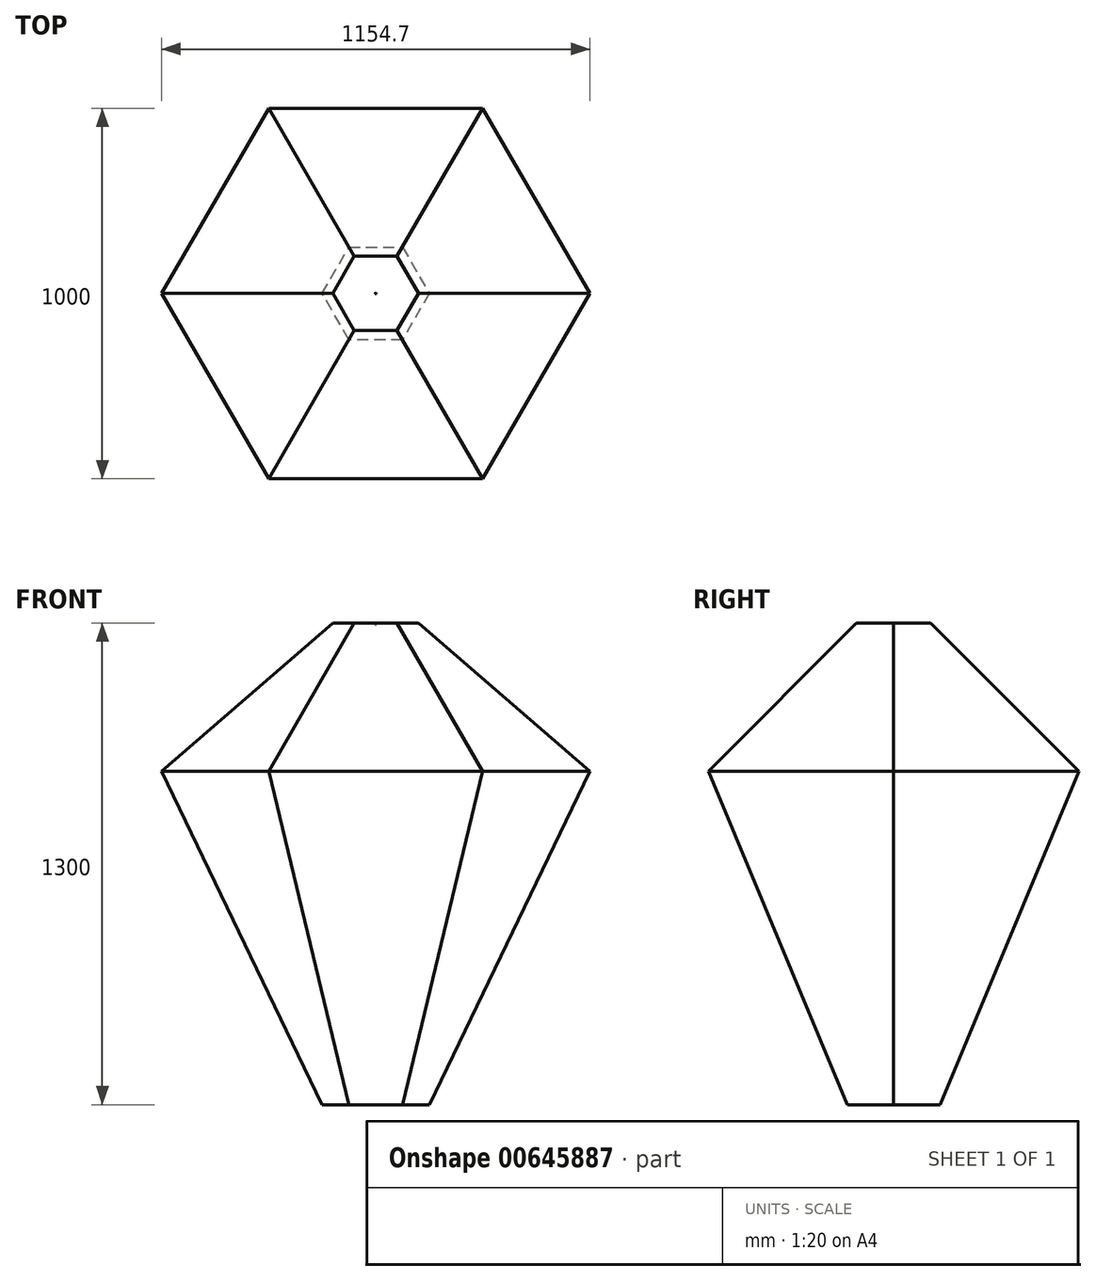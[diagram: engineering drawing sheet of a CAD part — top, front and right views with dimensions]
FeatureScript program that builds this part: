
annotation { "Feature Type Name" : "Feature", "Feature Type Description" : "" }
export const myFeature = defineFeature(function(context is Context, id is Id, definition is map)
    precondition{}
    {
        {
            assignVariable(context, id + "F0", {"name" : "Scale", "anyValue" : 1});
        }
        {
            var Q0;
            Q0=qCreatedBy(makeId("Top.planeOp"),FACE);
            var sketch = newSketch(context, id + "F1", { "sketchPlane" : qUnion([Q0])});
            skCircle(sketch, "E0.cCircle", {"center": v(0, 0) * mm, "radius": 500 * mm, "construction": true});
            skLineSegment(sketch, "E0.0", {"start": v(-288.68, 500) * mm, "end": v(288.68, 500) * mm});
            skLineSegment(sketch, "E0.1", {"start": v(288.68, 500) * mm, "end": v(577.35, 0) * mm});
            skLineSegment(sketch, "E0.2", {"start": v(577.35, 0) * mm, "end": v(288.68, -500) * mm});
            skLineSegment(sketch, "E0.3", {"start": v(288.68, -500) * mm, "end": v(-288.68, -500) * mm});
            skLineSegment(sketch, "E0.4", {"start": v(-288.68, -500) * mm, "end": v(-577.35, 0) * mm});
            skLineSegment(sketch, "E0.5", {"start": v(-577.35, 0) * mm, "end": v(-288.68, 500) * mm});
            skPoint(sketch, "E0.0.midPoint", {"position": v(0, 500) * mm});
            skSolve(sketch);
        }
        {
            var Q0;
            Q0=qCreatedBy(makeId("Top.planeOp"),FACE);
            cPlane(context, id + "F2", {"entities" : qUnion([Q0]), "cplaneType" : CPlaneType.OFFSET, "offset" : getVariable(context, 'Scale') * 400 * mm, "width" : 150 * mm, "height" : 150 * mm});
        }
        {
            var Q0;
            Q0=qCreatedBy(id+"F2.planeOp",FACE);
            var sketch = newSketch(context, id + "F3", { "sketchPlane" : qUnion([Q0])});
            skCircle(sketch, "E1.cCircle", {"center": v(0, 0) * mm, "radius": 100 * mm, "construction": true});
            skLineSegment(sketch, "E1.0", {"start": v(-57.74, 100) * mm, "end": v(57.74, 100) * mm});
            skLineSegment(sketch, "E1.1", {"start": v(57.74, 100) * mm, "end": v(115.47, 0) * mm});
            skLineSegment(sketch, "E1.2", {"start": v(115.47, 0) * mm, "end": v(57.74, -100) * mm});
            skLineSegment(sketch, "E1.3", {"start": v(57.74, -100) * mm, "end": v(-57.74, -100) * mm});
            skLineSegment(sketch, "E1.4", {"start": v(-57.74, -100) * mm, "end": v(-115.47, 0) * mm});
            skLineSegment(sketch, "E1.5", {"start": v(-115.47, 0) * mm, "end": v(-57.74, 100) * mm});
            skPoint(sketch, "E1.0.midPoint", {"position": v(0, 100) * mm});
            skSolve(sketch);
        }
        {
            var Q0;
            Q0=qCreatedBy(makeId("Top.planeOp"),FACE);
            cPlane(context, id + "F4", {"entities" : qUnion([Q0]), "cplaneType" : CPlaneType.OFFSET, "offset" : getVariable(context, 'Scale') * 900 * mm, "oppositeDirection" : true, "width" : 150 * mm, "height" : 150 * mm});
        }
        {
            var Q0;
            Q0=qCreatedBy(id+"F4.planeOp",FACE);
            var sketch = newSketch(context, id + "F5", { "sketchPlane" : qUnion([Q0])});
            skCircle(sketch, "E2.cCircle", {"center": v(0, 0) * mm, "radius": 125 * mm, "construction": true});
            skLineSegment(sketch, "E2.0", {"start": v(72.17, -125) * mm, "end": v(-72.17, -125) * mm});
            skLineSegment(sketch, "E2.1", {"start": v(-72.17, -125) * mm, "end": v(-144.34, 0) * mm});
            skLineSegment(sketch, "E2.2", {"start": v(-144.34, 0) * mm, "end": v(-72.17, 125) * mm});
            skLineSegment(sketch, "E2.3", {"start": v(-72.17, 125) * mm, "end": v(72.17, 125) * mm});
            skLineSegment(sketch, "E2.4", {"start": v(72.17, 125) * mm, "end": v(144.34, 0) * mm});
            skLineSegment(sketch, "E2.5", {"start": v(144.34, 0) * mm, "end": v(72.17, -125) * mm});
            skPoint(sketch, "E2.0.midPoint", {"position": v(0, -125) * mm});
            skSolve(sketch);
        }
        {
            var Q0;
            Q0=makeQuery(id+"F1.imprint","IMPRINT",FACE,{"disambiguationData":[TD([[makeQuery(id+"F1.imprint","IMPRINT",EDGE,{"derivedFrom":sQuery(id+"F1.wireOp",EDGE,"E0.0")}),-1.0]])]});
            var Q1;
            Q1=makeQuery(id+"F3.imprint","IMPRINT",FACE,{"disambiguationData":[TD([[makeQuery(id+"F3.imprint","IMPRINT",EDGE,{"derivedFrom":sQuery(id+"F3.wireOp",EDGE,"E1.0")}),-1.0]])]});
            loft(context, id + "F6", {"sheetProfilesArray" : [{ "sheetProfileEntities" : qUnion([Q0]) }, { "sheetProfileEntities" : qUnion([Q1]) }]});
        }
        {
            var Q1;
            Q1=makeQuery(id+"F5.imprint","IMPRINT",FACE,{"disambiguationData":[TD([[makeQuery(id+"F5.imprint","IMPRINT",EDGE,{"derivedFrom":sQuery(id+"F5.wireOp",EDGE,"E2.0")}),-1.0]])]});
            var Q2;
            Q2=makeQuery(id+"F6.opLoft","CAP_FACE",FACE,{"disambiguationData":[OSD([makeQuery(id+"F1.imprint","IMPRINT",FACE,{"disambiguationData":[TD([[makeQuery(id+"F1.imprint","IMPRINT",EDGE,{"derivedFrom":sQuery(id+"F1.wireOp",EDGE,"E0.0")}),-1.0]])]})])],"isStart":true});
            loft(context, id + "F7", {"operationType" : NewBodyOperationType.ADD, "sheetProfilesArray" : [{ "sheetProfileEntities" : qUnion([Q1]) }, { "sheetProfileEntities" : qUnion([Q2]) }]});
        }
        {
            var Q0;
            Q0=makeQuery(id+"F6.opLoft","CAP_FACE",FACE,{"disambiguationData":[OSD([makeQuery(id+"F3.imprint","IMPRINT",FACE,{"disambiguationData":[TD([[makeQuery(id+"F3.imprint","IMPRINT",EDGE,{"derivedFrom":sQuery(id+"F3.wireOp",EDGE,"E1.0")}),-1.0]])]})])],"isStart":true});
            var sketch = newSketch(context, id + "F8", { "sketchPlane" : qUnion([Q0])});
            skCircle(sketch, "E3", {"center": v(0, 0) * mm, "radius": 1 * mm});
            skSolve(sketch);
        }
        {
            var Q0;
            Q0=makeQuery(id+"F8.imprint","IMPRINT",FACE,{"disambiguationData":[TD([[makeQuery(id+"F8.imprint","IMPRINT",EDGE,{"derivedFrom":sQuery(id+"F8.wireOp",EDGE,"E3")}),1.0]])]});
            extrude(context, id + "F9", {"entities" : qUnion([Q0]), "operationType" : NewBodyOperationType.REMOVE, "oppositeDirection" : true, "depth" : 5 * mm, "offsetDistance" : 25 * mm});
        }
        {
            var Q0;
            Q0=makeQuery(id+"F6.opLoft","CAP_FACE",FACE,{"disambiguationData":[OSD([makeQuery(id+"F3.imprint","IMPRINT",FACE,{"disambiguationData":[TD([[makeQuery(id+"F3.imprint","IMPRINT",EDGE,{"derivedFrom":sQuery(id+"F3.wireOp",EDGE,"E1.0")}),-1.0]])]})])],"isStart":true});
            var sketch = newSketch(context, id + "F10", { "sketchPlane" : qUnion([Q0])});
            skCircle(sketch, "E4", {"center": v(57.74, -100) * mm, "radius": 15 * mm});
            skSolve(sketch);
        }
        {
            var Q0;
            {var subQ0=sQuery(id+"F1.wireOp",EDGE,"E0.3");var subQ1=sQuery(id+"F1.wireOp",EDGE,"E0.2");Q0=makeQuery(id+"F7.boolean.opBoolean","MERGE",VERTEX,{"derivedFrom":[makeQuery(id+"F6.opLoft","MID_CAP_VERTEX",VERTEX,{"disambiguationData":[OSD([subQ1,subQ0])],"capPos":0.0}),makeQuery(id+"F7.opLoft","MID_CAP_VERTEX",VERTEX,{"disambiguationData":[OSD([subQ1,subQ0])],"capPos":1.0})]});}
            var Q1;
            {var subQ0=sQuery(id+"F1.wireOp",EDGE,"E0.4");var subQ1=sQuery(id+"F1.wireOp",EDGE,"E0.3");var subQ2=sQuery(id+"F1.wireOp",EDGE,"E0.2");Q1=makeQuery(id+"F7.boolean.opBoolean","MERGE",EDGE,{"derivedFrom":[makeQuery(id+"F6.opLoft","MID_CAP_EDGE",EDGE,{"disambiguationData":[OSD([subQ2,subQ1,subQ0])],"capPos":0.0}),makeQuery(id+"F7.opLoft","MID_CAP_EDGE",EDGE,{"disambiguationData":[OSD([subQ2,subQ1,subQ0])],"capPos":1.0})]});}
            cPlane(context, id + "F11", {"entities" : qUnion([Q0, Q1]), "cplaneType" : CPlaneType.CURVE_POINT, "offset" : 25 * mm, "width" : 150 * mm, "height" : 150 * mm});
        }
        {
            var Q0;
            Q0=qCreatedBy(id+"F11.planeOp",FACE);
            var sketch = newSketch(context, id + "F12", { "sketchPlane" : qUnion([Q0])});
            skCircle(sketch, "E5", {"center": v(-500, 0) * mm, "radius": 10 * mm});
            skSolve(sketch);
        }
        {
            var Q0;
            Q0=qCreatedBy(makeId("Front.planeOp"),FACE);
            var sketch = newSketch(context, id + "F13", { "sketchPlane" : qUnion([Q0])});
            skLineSegment(sketch, "E6", {"start": v(0, 0) * mm, "end": v(0, 7.92) * mm, "construction": true});
            skSolve(sketch);
        }
        {
            var Q0;
            Q0=makeQuery(id+"F6.opLoft","SWEPT_BODY",BODY,{"disambiguationData":[OSD([makeQuery(id+"F1.imprint","IMPRINT",FACE,{"disambiguationData":[TD([[makeQuery(id+"F1.imprint","IMPRINT",EDGE,{"derivedFrom":sQuery(id+"F1.wireOp",EDGE,"E0.0")}),-1.0]])]}),makeQuery(id+"F3.imprint","IMPRINT",FACE,{"disambiguationData":[TD([[makeQuery(id+"F3.imprint","IMPRINT",EDGE,{"derivedFrom":sQuery(id+"F3.wireOp",EDGE,"E1.0")}),-1.0]])]})])]});
            var Q1;
            Q1=makeQuery(id+"FsViyaIz4K34HAL_1.opSweep","SWEPT_BODY",BODY,{"disambiguationData":[OSD([sQuery(id+"F1.wireOp",EDGE,"E0.2"),sQuery(id+"F1.wireOp",EDGE,"E0.3"),sQuery(id+"F5.wireOp",EDGE,"E2.0"),sQuery(id+"F5.wireOp",EDGE,"E2.5"),sQuery(id+"F10.wireOp",EDGE,"E4")])]});
            var Q2;
            Q2=sQuery(id+"F13.wireOp",EDGE,"E6");
            circularPattern(context, id + "F14", {"entities" : qUnion([Q0, Q1]), "axis" : qUnion([Q2]), "angle" : 360 * degree, "instanceCount" : 6, "equalSpace" : true});
        }
        {
            var Q0;
            Q0=makeQuery(id+"F6.opLoft","MID_CAP_EDGE",EDGE,{"disambiguationData":[OSD([sQuery(id+"F3.wireOp",EDGE,"E1.2"),sQuery(id+"F3.wireOp",EDGE,"E1.3"),sQuery(id+"F3.wireOp",EDGE,"E1.4")])],"capPos":1.0});
            var Q1;
            Q1=makeQuery(id+"F6.opLoft","MID_CAP_VERTEX",VERTEX,{"disambiguationData":[OSD([sQuery(id+"F3.wireOp",EDGE,"E1.2"),sQuery(id+"F3.wireOp",EDGE,"E1.3")])],"capPos":1.0});
            cPlane(context, id + "F15", {"entities" : qUnion([Q0, Q1]), "cplaneType" : CPlaneType.CURVE_POINT, "offset" : 25 * mm, "width" : 150 * mm, "height" : 150 * mm});
        }
        {
            var Q0;
            Q0=qCreatedBy(id+"F15.planeOp",FACE);
            var sketch = newSketch(context, id + "F16", { "sketchPlane" : qUnion([Q0])});
            skCircle(sketch, "E7", {"center": v(-100, 400) * mm, "radius": 0.25 * mm});
            skSolve(sketch);
        }
        {
            var Q0;
            Q0=makeQuery(id+"F7.opLoft","MID_CAP_EDGE",EDGE,{"disambiguationData":[OSD([sQuery(id+"F5.wireOp",EDGE,"E2.3"),sQuery(id+"F5.wireOp",EDGE,"E2.4"),sQuery(id+"F5.wireOp",EDGE,"E2.5")])],"capPos":0.0});
            var Q1;
            Q1=makeQuery(id+"F7.opLoft","MID_CAP_VERTEX",VERTEX,{"disambiguationData":[OSD([sQuery(id+"F5.wireOp",EDGE,"E2.3"),sQuery(id+"F5.wireOp",EDGE,"E2.4")])],"capPos":0.0});
            cPlane(context, id + "F17", {"entities" : qUnion([Q0, Q1]), "cplaneType" : CPlaneType.LINE_POINT, "offset" : 25 * mm, "width" : 150 * mm, "height" : 150 * mm});
        }
    });
